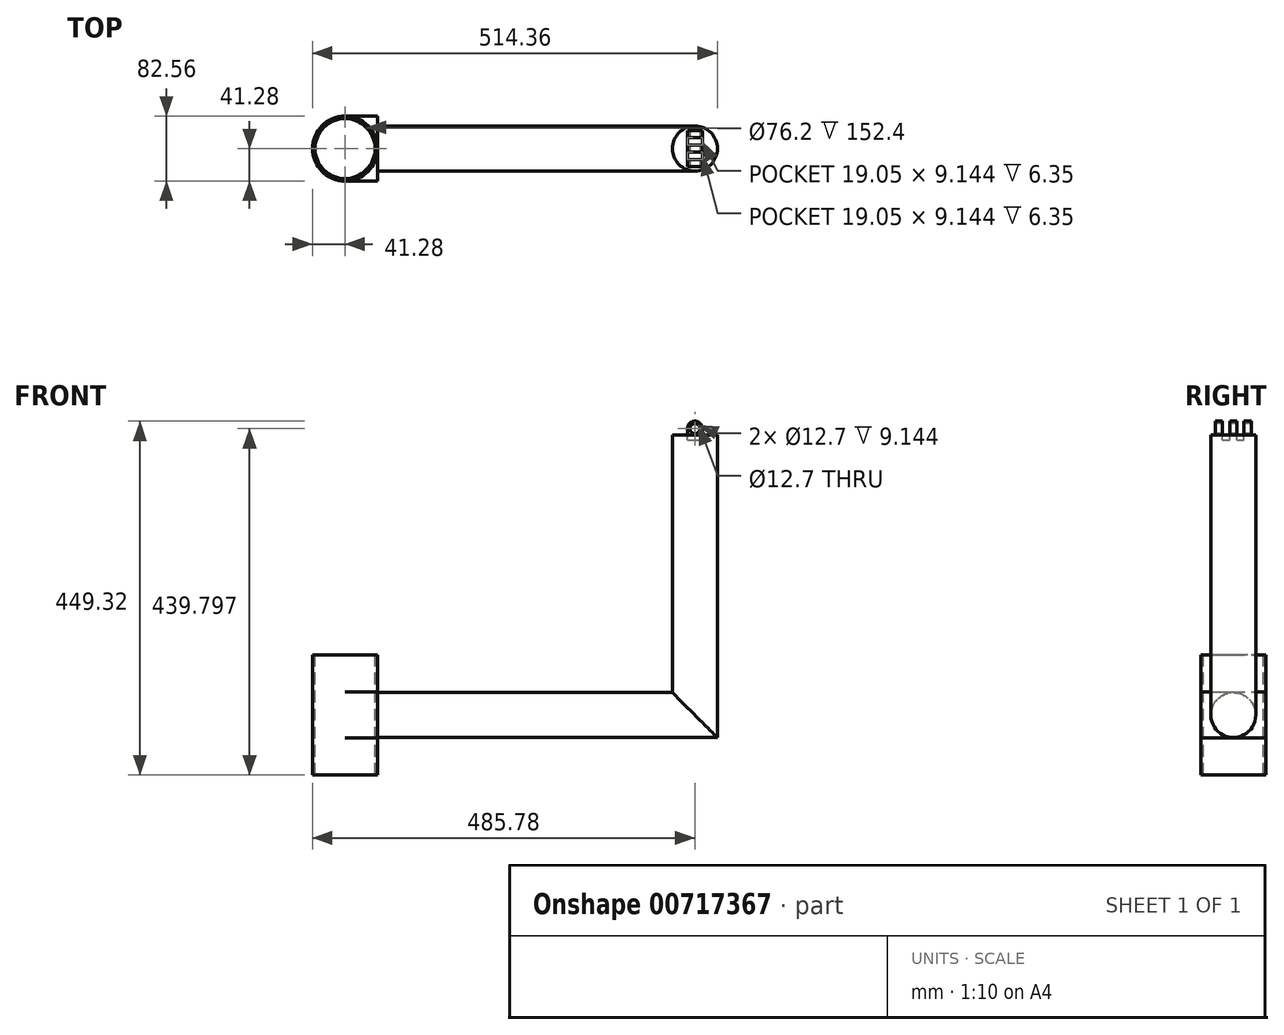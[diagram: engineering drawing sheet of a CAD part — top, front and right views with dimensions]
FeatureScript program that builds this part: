
annotation { "Feature Type Name" : "Feature", "Feature Type Description" : "" }
export const myFeature = defineFeature(function(context is Context, id is Id, definition is map)
    precondition{}
    {
        {
            var Q0;
            Q0=qCreatedBy(makeId("Top.planeOp"),FACE);
            var sketch = newSketch(context, id + "F0", { "sketchPlane" : qUnion([Q0])});
            skLineSegment(sketch, "E0.bottom", {"start": v(41.28, -41.27) * mm, "end": v(-41.28, -41.28) * mm});
            skLineSegment(sketch, "E0.top", {"start": v(41.28, 41.28) * mm, "end": v(-41.28, 41.27) * mm});
            skLineSegment(sketch, "E0.left", {"start": v(41.28, -41.27) * mm, "end": v(41.28, 41.28) * mm});
            skLineSegment(sketch, "E0.right", {"start": v(-41.28, -41.28) * mm, "end": v(-41.28, 41.27) * mm});
            skPoint(sketch, "E0.middle", {"position": v(0, 0) * mm});
            skSolve(sketch);
        }
        {
            var Q0;
            Q0=makeQuery(id+"F0.imprint","IMPRINT",FACE,{"disambiguationData":[TD([[makeQuery(id+"F0.imprint","IMPRINT",EDGE,{"derivedFrom":sQuery(id+"F0.wireOp",EDGE,"E0.bottom")}),-1.0]])]});
            extrude(context, id + "F1", {"entities" : qUnion([Q0]), "depth" : 152.4 * mm, "offsetDistance" : 25.4 * mm});
        }
        {
            var Q0;
            Q0=makeQuery(id+"F1.opExtrude","SWEPT_FACE",FACE,{"disambiguationData":[OSD([sQuery(id+"F0.wireOp",EDGE,"E0.left")])]});
            var sketch = newSketch(context, id + "F2", { "sketchPlane" : qUnion([Q0])});
            skCircle(sketch, "E1", {"center": v(0, 76.73) * mm, "radius": 28.58 * mm});
            skSolve(sketch);
        }
        {
            var Q0;
            Q0=makeQuery(id+"F2.imprint","IMPRINT",FACE,{"disambiguationData":[TD([[makeQuery(id+"F2.imprint","IMPRINT",EDGE,{"derivedFrom":sQuery(id+"F2.wireOp",EDGE,"E1")}),1.0]])]});
            extrude(context, id + "F3", {"entities" : qUnion([Q0]), "operationType" : NewBodyOperationType.ADD, "oppositeDirection" : true, "depth" : 19.05 * mm, "offsetDistance" : 25.4 * mm});
        }
        {
            var Q0;
            Q0=makeQuery(id+"F1.opExtrude","SWEPT_FACE",FACE,{"disambiguationData":[OSD([sQuery(id+"F0.wireOp",EDGE,"E0.left")])]});
            var sketch = newSketch(context, id + "F4", { "sketchPlane" : qUnion([Q0])});
            skCircle(sketch, "E2", {"center": v(0, 75.81) * mm, "radius": 28.58 * mm});
            skSolve(sketch);
        }
        {
            var Q0;
            Q0=makeQuery(id+"F4.imprint","IMPRINT",FACE,{"disambiguationData":[TD([[makeQuery(id+"F4.imprint","IMPRINT",EDGE,{"derivedFrom":sQuery(id+"F4.wireOp",EDGE,"E2")}),1.0]])]});
            extrude(context, id + "F5", {"entities" : qUnion([Q0]), "operationType" : NewBodyOperationType.ADD, "depth" : 431.8 * mm, "offsetDistance" : 25.4 * mm});
        }
        {
            var Q0;
            Q0=makeQuery(id+"F1.opExtrude","CAP_FACE",FACE,{"disambiguationData":[OSD([sQuery(id+"F0.wireOp",EDGE,"E0.bottom"),sQuery(id+"F0.wireOp",EDGE,"E0.top"),sQuery(id+"F0.wireOp",EDGE,"E0.left"),sQuery(id+"F0.wireOp",EDGE,"E0.right")])],"isStart":false});
            var sketch = newSketch(context, id + "F6", { "sketchPlane" : qUnion([Q0])});
            skCircle(sketch, "E3", {"center": v(0, 0) * mm, "radius": 38.1 * mm});
            skSolve(sketch);
        }
        {
            var Q0;
            Q0=makeQuery(id+"F6.imprint","IMPRINT",FACE,{"disambiguationData":[TD([[makeQuery(id+"F6.imprint","IMPRINT",EDGE,{"derivedFrom":sQuery(id+"F6.wireOp",EDGE,"E3")}),1.0]])]});
            extrude(context, id + "F7", {"entities" : qUnion([Q0]), "operationType" : NewBodyOperationType.REMOVE, "oppositeDirection" : true, "depth" : 177.8 * mm, "offsetDistance" : 25.4 * mm});
        }
        {
            var Q0;
            Q0=makeQuery(id+"F1.opExtrude","CAP_FACE",FACE,{"disambiguationData":[OSD([sQuery(id+"F0.wireOp",EDGE,"E0.bottom"),sQuery(id+"F0.wireOp",EDGE,"E0.top"),sQuery(id+"F0.wireOp",EDGE,"E0.left"),sQuery(id+"F0.wireOp",EDGE,"E0.right")])],"isStart":true});
            var sketch = newSketch(context, id + "F8", { "sketchPlane" : qUnion([Q0])});
            skCircle(sketch, "E4", {"center": v(0, 0) * mm, "radius": 41.28 * mm});
            skSolve(sketch);
        }
        {
            var Q0;
            {var subQ0=sQuery(id+"F8.wireOp",EDGE,"E4");var subQ1=makeQuery(id+"F1.opExtrude","CAP_EDGE",EDGE,{"disambiguationData":[OSD([sQuery(id+"F0.wireOp",EDGE,"E0.left")])],"isStart":true});var subQ2=makeQuery(id+"F8.imprint","INTERSECT",VERTEX,{"derivedFrom":[subQ1,subQ0]});Q0=makeQuery(id+"F8.imprint","IMPRINT",FACE,{"disambiguationData":[TD([[makeQuery(id+"F8.imprint","IMPRINT",EDGE,{"disambiguationData":[TD([[subQ2,1.0]])],"derivedFrom":subQ0}),-1.0]])]});}
            var Q1;
            {var subQ0=sQuery(id+"F8.wireOp",EDGE,"E4");var subQ1=makeQuery(id+"F1.opExtrude","CAP_EDGE",EDGE,{"disambiguationData":[OSD([sQuery(id+"F0.wireOp",EDGE,"E0.bottom")])],"isStart":true});var subQ2=makeQuery(id+"F8.imprint","INTERSECT",VERTEX,{"derivedFrom":[subQ1,subQ0]});Q1=makeQuery(id+"F8.imprint","IMPRINT",FACE,{"disambiguationData":[TD([[makeQuery(id+"F8.imprint","IMPRINT",EDGE,{"disambiguationData":[TD([[subQ2,1.0]])],"derivedFrom":subQ0}),-1.0]])]});}
            extrude(context, id + "F9", {"entities" : qUnion([Q0, Q1]), "operationType" : NewBodyOperationType.REMOVE, "oppositeDirection" : true, "depth" : 47 * mm, "offsetDistance" : 25.4 * mm});
        }
        {
            var Q0;
            Q0=makeQuery(id+"F1.opExtrude","CAP_FACE",FACE,{"disambiguationData":[OSD([sQuery(id+"F0.wireOp",EDGE,"E0.bottom"),sQuery(id+"F0.wireOp",EDGE,"E0.top"),sQuery(id+"F0.wireOp",EDGE,"E0.left"),sQuery(id+"F0.wireOp",EDGE,"E0.right")])],"isStart":true});
            var sketch = newSketch(context, id + "F10", { "sketchPlane" : qUnion([Q0])});
            skCircle(sketch, "E5", {"center": v(0, 0) * mm, "radius": 41.28 * mm});
            skSolve(sketch);
        }
        {
            var Q0;
            {var subQ1=makeQuery(id+"F1.opExtrude","CAP_EDGE",EDGE,{"disambiguationData":[OSD([sQuery(id+"F0.wireOp",EDGE,"E0.bottom")])],"isStart":true});Q0=makeQuery(id+"F10.imprint","IMPRINT",FACE,{"disambiguationData":[TD([[makeQuery(id+"F10.imprint","IMPRINT",EDGE,{"derivedFrom":subQ1}),1.0]])]});}
            var Q1;
            {var subQ1=makeQuery(id+"F1.opExtrude","CAP_EDGE",EDGE,{"disambiguationData":[OSD([sQuery(id+"F0.wireOp",EDGE,"E0.top")])],"isStart":true});Q1=makeQuery(id+"F10.imprint","IMPRINT",FACE,{"disambiguationData":[TD([[makeQuery(id+"F10.imprint","IMPRINT",EDGE,{"derivedFrom":subQ1}),-1.0]])]});}
            extrude(context, id + "F11", {"entities" : qUnion([Q0, Q1]), "operationType" : NewBodyOperationType.REMOVE, "oppositeDirection" : true, "depth" : 177.8 * mm, "offsetDistance" : 25.4 * mm});
        }
        {
            var Q0;
            Q0=makeQuery(id+"F1.opExtrude","CAP_FACE",FACE,{"disambiguationData":[OSD([sQuery(id+"F0.wireOp",EDGE,"E0.bottom"),sQuery(id+"F0.wireOp",EDGE,"E0.top"),sQuery(id+"F0.wireOp",EDGE,"E0.left"),sQuery(id+"F0.wireOp",EDGE,"E0.right")])],"isStart":false});
            var sketch = newSketch(context, id + "F12", { "sketchPlane" : qUnion([Q0])});
            skCircle(sketch, "E6", {"center": v(0, 0) * mm, "radius": 41.28 * mm});
            skSolve(sketch);
        }
        {
            var Q0;
            {var subQ1=makeQuery(id+"F1.opExtrude","CAP_EDGE",EDGE,{"disambiguationData":[OSD([sQuery(id+"F0.wireOp",EDGE,"E0.top")])],"isStart":false});Q0=makeQuery(id+"F12.imprint","IMPRINT",FACE,{"disambiguationData":[TD([[makeQuery(id+"F12.imprint","IMPRINT",EDGE,{"derivedFrom":subQ1}),1.0]])]});}
            var Q1;
            {var subQ1=makeQuery(id+"F1.opExtrude","CAP_EDGE",EDGE,{"disambiguationData":[OSD([sQuery(id+"F0.wireOp",EDGE,"E0.bottom")])],"isStart":false});Q1=makeQuery(id+"F12.imprint","IMPRINT",FACE,{"disambiguationData":[TD([[makeQuery(id+"F12.imprint","IMPRINT",EDGE,{"derivedFrom":subQ1}),-1.0]])]});}
            extrude(context, id + "F13", {"entities" : qUnion([Q0, Q1]), "operationType" : NewBodyOperationType.REMOVE, "oppositeDirection" : true, "depth" : 47 * mm, "offsetDistance" : 25.4 * mm});
        }
        {
            var Q0;
            Q0=makeQuery(id+"F5.opExtrude","CAP_FACE",FACE,{"disambiguationData":[OSD([sQuery(id+"F4.wireOp",EDGE,"E2")])],"isStart":false});
            var sketch = newSketch(context, id + "F14", { "sketchPlane" : qUnion([Q0])});
            skLineSegment(sketch, "E7", {"start": v(-28.58, 75.81) * mm, "end": v(28.58, 75.81) * mm});
            skArc(sketch, "E8", {"start": v(28.58, 75.81) * mm, "mid": v(0, 104.39) * mm, "end": v(-28.58, 75.81) * mm});
            skSolve(sketch);
        }
        {
            var Q0;
            Q0=makeQuery(id+"F14.imprint","IMPRINT",FACE,{"disambiguationData":[TD([[makeQuery(id+"F14.imprint","IMPRINT",EDGE,{"derivedFrom":sQuery(id+"F14.wireOp",EDGE,"E7")}),1.0]])]});
            extrude(context, id + "F15", {"entities" : qUnion([Q0]), "operationType" : NewBodyOperationType.REMOVE, "oppositeDirection" : true, "depth" : 28.57 * mm, "offsetDistance" : 25.4 * mm});
        }
        {
            var Q0;
            Q0=makeQuery(id+"F15.boolean.opBoolean","COPY",FACE,{"derivedFrom":makeQuery(id+"F15.opExtrude","SWEPT_FACE",FACE,{"disambiguationData":[OSD([sQuery(id+"F14.wireOp",EDGE,"E7")])]})});
            var sketch = newSketch(context, id + "F16", { "sketchPlane" : qUnion([Q0])});
            skLineSegment(sketch, "E9", {"start": v(444.5, -28.58) * mm, "end": v(444.5, 28.57) * mm});
            skArc(sketch, "E10", {"start": v(444.5, -28.58) * mm, "mid": v(473.08, 0) * mm, "end": v(444.5, 28.57) * mm});
            skSolve(sketch);
        }
        {
            var Q0;
            {var subQ0=sQuery(id+"F16.wireOp",EDGE,"E9");Q0=makeQuery(id+"F16.imprint","IMPRINT",FACE,{"disambiguationData":[TD([[makeQuery(id+"F16.imprint","IMPRINT",EDGE,{"derivedFrom":subQ0}),-1.0]])]});}
            extrude(context, id + "F17", {"entities" : qUnion([Q0]), "operationType" : NewBodyOperationType.ADD, "depth" : 355.6 * mm, "offsetDistance" : 25.4 * mm});
        }
        {
            var Q0;
            Q0=makeQuery(id+"F17.boolean.opBoolean","SPLIT",FACE,{"disambiguationData":[OD(0.0)],"derivedFrom":makeQuery(id+"F15.boolean.opBoolean","COPY",FACE,{"derivedFrom":makeQuery(id+"F15.opExtrude","SWEPT_FACE",FACE,{"disambiguationData":[OSD([sQuery(id+"F14.wireOp",EDGE,"E7")])]})})});
            var Q1;
            Q1=makeQuery(id+"F17.boolean.opBoolean","SPLIT",FACE,{"disambiguationData":[OD(1.0)],"derivedFrom":makeQuery(id+"F15.boolean.opBoolean","COPY",FACE,{"derivedFrom":makeQuery(id+"F15.opExtrude","SWEPT_FACE",FACE,{"disambiguationData":[OSD([sQuery(id+"F14.wireOp",EDGE,"E7")])]})})});
            extrude(context, id + "F18", {"entities" : qUnion([Q0, Q1]), "operationType" : NewBodyOperationType.REMOVE, "oppositeDirection" : true, "depth" : 50.8 * mm, "offsetDistance" : 25.4 * mm});
        }
        {
            var Q0;
            Q0=makeQuery(id+"F17.opExtrude","CAP_FACE",FACE,{"disambiguationData":[OSD([sQuery(id+"F16.wireOp",EDGE,"E9"),sQuery(id+"F16.wireOp",EDGE,"E10")])],"isStart":false});
            var sketch = newSketch(context, id + "F19", { "sketchPlane" : qUnion([Q0])});
            skCircle(sketch, "E11", {"center": v(444.5, 0) * mm, "radius": 28.58 * mm});
            skSolve(sketch);
        }
        {
            var Q0;
            {var subQ1=makeQuery(id+"F17.opExtrude","CAP_EDGE",EDGE,{"disambiguationData":[OSD([sQuery(id+"F16.wireOp",EDGE,"E9")])],"isStart":false});Q0=makeQuery(id+"F19.imprint","IMPRINT",FACE,{"disambiguationData":[TD([[makeQuery(id+"F19.imprint","IMPRINT",EDGE,{"derivedFrom":subQ1}),1.0]])]});}
            extrude(context, id + "F20", {"entities" : qUnion([Q0]), "operationType" : NewBodyOperationType.ADD, "oppositeDirection" : true, "depth" : 355.6 * mm, "offsetDistance" : 25.4 * mm});
        }
        {
            var Q0;
            {var subQ0=sQuery(id+"F16.wireOp",EDGE,"E9");Q0=makeQuery(id+"F20.boolean.opBoolean","MERGE",FACE,{"derivedFrom":[makeQuery(id+"F17.opExtrude","CAP_FACE",FACE,{"disambiguationData":[OSD([subQ0,sQuery(id+"F16.wireOp",EDGE,"E10")])],"isStart":false}),makeQuery(id+"F20.opExtrude","CAP_FACE",FACE,{"disambiguationData":[OSD([subQ0,sQuery(id+"F19.wireOp",EDGE,"E11")])],"isStart":true})]});}
            var sketch = newSketch(context, id + "F21", { "sketchPlane" : qUnion([Q0])});
            skLineSegment(sketch, "E12", {"start": v(415.93, -0.6) * mm, "end": v(415.93, 0.6) * mm, "construction": true});
            skLineSegment(sketch, "E13", {"start": v(415.93, 0) * mm, "end": v(473.08, 0) * mm, "construction": true});
            skPoint(sketch, "E14.middle", {"position": v(415.93, 0) * mm});
            skLineSegment(sketch, "E15.bottom", {"start": v(454.03, -22.86) * mm, "end": v(434.98, -22.86) * mm});
            skLineSegment(sketch, "E15.top", {"start": v(454.03, 22.86) * mm, "end": v(434.98, 22.86) * mm});
            skLineSegment(sketch, "E15.left", {"start": v(454.03, -22.86) * mm, "end": v(454.03, 22.86) * mm});
            skLineSegment(sketch, "E15.right", {"start": v(434.98, -22.86) * mm, "end": v(434.98, 22.86) * mm});
            skPoint(sketch, "E15.middle", {"position": v(444.5, 0) * mm});
            skSolve(sketch);
        }
        {
            var Q0;
            Q0=makeQuery(id+"F21.imprint","IMPRINT",FACE,{"disambiguationData":[TD([[makeQuery(id+"F21.imprint","IMPRINT",EDGE,{"derivedFrom":sQuery(id+"F21.wireOp",EDGE,"E14.bottom")}),1.0]])]});
            var Q1;
            Q1=makeQuery(id+"F21.imprint","IMPRINT",FACE,{"disambiguationData":[TD([[makeQuery(id+"F21.imprint","IMPRINT",EDGE,{"derivedFrom":sQuery(id+"F21.wireOp",EDGE,"E15.bottom")}),-1.0]])]});
            extrude(context, id + "F22", {"entities" : qUnion([Q0, Q1]), "operationType" : NewBodyOperationType.ADD, "depth" : 19.05 * mm, "offsetDistance" : 25.4 * mm});
        }
        {
            var Q0;
            Q0=makeQuery(id+"F22.opExtrude","CAP_FACE",FACE,{"disambiguationData":[OSD([sQuery(id+"F21.wireOp",EDGE,"E15.bottom"),sQuery(id+"F21.wireOp",EDGE,"E15.top"),sQuery(id+"F21.wireOp",EDGE,"E15.left"),sQuery(id+"F21.wireOp",EDGE,"E15.right")])],"isStart":false});
            var sketch = newSketch(context, id + "F23", { "sketchPlane" : qUnion([Q0])});
            skLineSegment(sketch, "E16", {"start": v(257.18, -22.86) * mm, "end": v(257.18, -13.72) * mm, "construction": true});
            skLineSegment(sketch, "E17", {"start": v(257.18, -13.72) * mm, "end": v(257.18, -4.57) * mm, "construction": true});
            skLineSegment(sketch, "E18", {"start": v(257.18, -4.57) * mm, "end": v(257.18, 4.57) * mm, "construction": true});
            skLineSegment(sketch, "E19", {"start": v(257.18, 4.57) * mm, "end": v(257.18, 13.72) * mm, "construction": true});
            skLineSegment(sketch, "E20", {"start": v(257.18, 13.72) * mm, "end": v(257.18, 22.86) * mm, "construction": true});
            skLineSegment(sketch, "E21.bottom", {"start": v(257.18, -13.72) * mm, "end": v(276.23, -13.72) * mm});
            skLineSegment(sketch, "E21.top", {"start": v(257.18, -4.57) * mm, "end": v(276.23, -4.57) * mm});
            skLineSegment(sketch, "E21.left", {"start": v(257.18, -13.72) * mm, "end": v(257.18, -4.57) * mm});
            skLineSegment(sketch, "E21.right", {"start": v(276.23, -13.72) * mm, "end": v(276.23, -4.57) * mm});
            skLineSegment(sketch, "E22.bottom", {"start": v(257.18, 4.57) * mm, "end": v(276.23, 4.57) * mm});
            skLineSegment(sketch, "E22.top", {"start": v(257.18, 13.72) * mm, "end": v(276.23, 13.72) * mm});
            skLineSegment(sketch, "E22.left", {"start": v(257.18, 4.57) * mm, "end": v(257.18, 13.72) * mm});
            skLineSegment(sketch, "E22.right", {"start": v(276.23, 4.57) * mm, "end": v(276.23, 13.72) * mm});
            skLineSegment(sketch, "E23", {"start": v(434.98, -22.86) * mm, "end": v(434.98, -13.72) * mm, "construction": true});
            skLineSegment(sketch, "E24", {"start": v(434.98, -4.57) * mm, "end": v(434.98, -13.72) * mm, "construction": true});
            skLineSegment(sketch, "E25", {"start": v(434.98, -4.57) * mm, "end": v(434.98, 4.57) * mm, "construction": true});
            skLineSegment(sketch, "E26", {"start": v(434.98, 4.57) * mm, "end": v(434.98, 13.72) * mm, "construction": true});
            skLineSegment(sketch, "E27", {"start": v(434.98, 13.72) * mm, "end": v(434.98, 22.86) * mm, "construction": true});
            skLineSegment(sketch, "E28", {"start": v(434.98, -13.72) * mm, "end": v(454.03, -13.72) * mm});
            skLineSegment(sketch, "E29", {"start": v(434.98, -4.57) * mm, "end": v(454.03, -4.57) * mm});
            skLineSegment(sketch, "E30", {"start": v(434.98, 4.57) * mm, "end": v(454.03, 4.57) * mm});
            skLineSegment(sketch, "E31", {"start": v(434.98, 13.72) * mm, "end": v(454.03, 13.72) * mm});
            skSolve(sketch);
        }
        {
            var Q0;
            {var subQ0=sQuery(id+"F23.wireOp",EDGE,"E28");Q0=makeQuery(id+"F23.imprint","IMPRINT",FACE,{"disambiguationData":[TD([[makeQuery(id+"F23.imprint","IMPRINT",EDGE,{"derivedFrom":subQ0}),1.0]])]});}
            var Q1;
            {var subQ0=sQuery(id+"F23.wireOp",EDGE,"E30");Q1=makeQuery(id+"F23.imprint","IMPRINT",FACE,{"disambiguationData":[TD([[makeQuery(id+"F23.imprint","IMPRINT",EDGE,{"derivedFrom":subQ0}),1.0]])]});}
            extrude(context, id + "F24", {"entities" : qUnion([Q0, Q1]), "operationType" : NewBodyOperationType.REMOVE, "oppositeDirection" : true, "depth" : 25.4 * mm, "offsetDistance" : 25.4 * mm});
        }
        {
            var Q0;
            Q0=makeQuery(id+"F22.opExtrude","SWEPT_FACE",FACE,{"disambiguationData":[OSD([sQuery(id+"F21.wireOp",EDGE,"E15.bottom")])]});
            var sketch = newSketch(context, id + "F25", { "sketchPlane" : qUnion([Q0])});
            skLineSegment(sketch, "E32", {"start": v(444.5, 450.46) * mm, "end": v(444.5, 439.8) * mm, "construction": true});
            skCircle(sketch, "E33", {"center": v(444.5, 439.8) * mm, "radius": 9.53 * mm});
            skCircle(sketch, "E34", {"center": v(444.5, 439.8) * mm, "radius": 6.35 * mm});
            skSolve(sketch);
        }
        {
            var Q0;
            {var subQ0=sQuery(id+"F25.wireOp",EDGE,"E33");var subQ1=sQuery(id+"F21.wireOp",EDGE,"E15.bottom");var subQ4=makeQuery(id+"F22.opExtrude","CAP_EDGE",EDGE,{"disambiguationData":[OSD([subQ1])],"isStart":true});var subQ5=makeQuery(id+"F25.imprint","INTERSECT",VERTEX,{"disambiguationData":[OD(0.0)],"derivedFrom":[subQ4,subQ0]});Q0=makeQuery(id+"F25.imprint","IMPRINT",FACE,{"disambiguationData":[TD([[makeQuery(id+"F25.imprint","IMPRINT",EDGE,{"disambiguationData":[TD([[subQ5,1.0]])],"derivedFrom":subQ0}),-1.0]])]});}
            var Q1;
            {var subQ1=sQuery(id+"F21.wireOp",EDGE,"E15.bottom");var subQ6=makeQuery(id+"F22.opExtrude","CAP_EDGE",EDGE,{"disambiguationData":[OSD([subQ1])],"isStart":false});Q1=makeQuery(id+"F25.imprint","IMPRINT",FACE,{"disambiguationData":[TD([[makeQuery(id+"F25.imprint","IMPRINT",EDGE,{"derivedFrom":subQ6}),1.0]])]});}
            var Q2;
            {var subQ0=sQuery(id+"F25.wireOp",EDGE,"E33");var subQ1=sQuery(id+"F21.wireOp",EDGE,"E15.bottom");var subQ4=makeQuery(id+"F22.opExtrude","CAP_EDGE",EDGE,{"disambiguationData":[OSD([subQ1])],"isStart":true});var subQ5=makeQuery(id+"F25.imprint","INTERSECT",VERTEX,{"disambiguationData":[OD(1.0)],"derivedFrom":[subQ4,subQ0]});Q2=makeQuery(id+"F25.imprint","IMPRINT",FACE,{"disambiguationData":[TD([[makeQuery(id+"F25.imprint","IMPRINT",EDGE,{"disambiguationData":[TD([[subQ5,-1.0]])],"derivedFrom":subQ0}),-1.0]])]});}
            var Q3;
            Q3=makeQuery(id+"F25.imprint","IMPRINT",FACE,{"disambiguationData":[TD([[makeQuery(id+"F25.imprint","IMPRINT",EDGE,{"derivedFrom":sQuery(id+"F25.wireOp",EDGE,"E34")}),1.0]])]});
            extrude(context, id + "F26", {"entities" : qUnion([Q0, Q1, Q2, Q3]), "operationType" : NewBodyOperationType.REMOVE, "oppositeDirection" : true, "depth" : 127 * mm, "offsetDistance" : 25.4 * mm});
        }
    });
